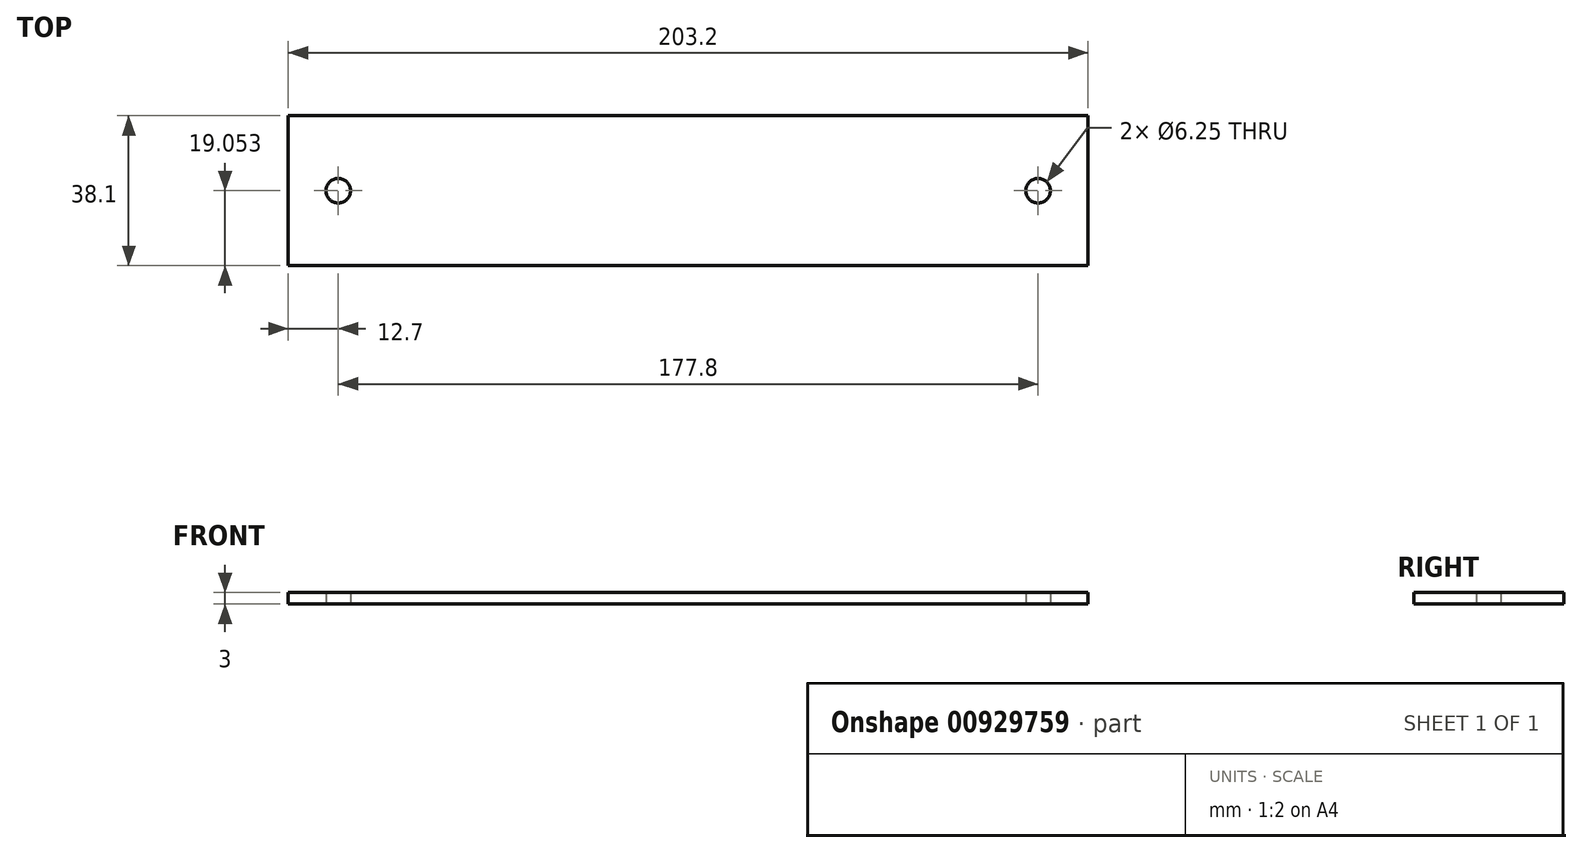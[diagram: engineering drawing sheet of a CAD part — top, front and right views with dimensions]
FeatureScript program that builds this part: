
annotation { "Feature Type Name" : "Feature", "Feature Type Description" : "" }
export const myFeature = defineFeature(function(context is Context, id is Id, definition is map)
    precondition{}
    {
        {
            var Q0;
            Q0=qCreatedBy(makeId("Top.planeOp"),FACE);
            var sketch = newSketch(context, id + "F0", { "sketchPlane" : qUnion([Q0])});
            skLineSegment(sketch, "E0.bottom", {"start": v(-107.28, 3.71) * mm, "end": v(95.92, 3.71) * mm});
            skLineSegment(sketch, "E0.top", {"start": v(-107.28, -34.39) * mm, "end": v(95.92, -34.39) * mm});
            skLineSegment(sketch, "E0.left", {"start": v(-107.28, 3.71) * mm, "end": v(-107.28, -34.39) * mm});
            skLineSegment(sketch, "E0.right", {"start": v(95.92, 3.71) * mm, "end": v(95.92, -34.39) * mm});
            skLineSegment(sketch, "E1", {"start": v(-107.28, -15.34) * mm, "end": v(95.92, -15.34) * mm});
            skPoint(sketch, "E2", {"position": v(-5.68, -15.34) * mm});
            skLineSegment(sketch, "E3", {"start": v(-5.68, -15.34) * mm, "end": v(95.92, -15.34) * mm});
            skPoint(sketch, "E4", {"position": v(45.12, -15.34) * mm});
            skLineSegment(sketch, "E5", {"start": v(45.12, -15.34) * mm, "end": v(95.92, -15.34) * mm});
            skPoint(sketch, "E6", {"position": v(70.52, -15.34) * mm});
            skLineSegment(sketch, "E7", {"start": v(70.52, -15.34) * mm, "end": v(95.92, -15.34) * mm});
            skPoint(sketch, "E8", {"position": v(83.22, -15.34) * mm});
            skCircle(sketch, "E9", {"center": v(83.22, -15.34) * mm, "radius": 3.12 * mm});
            skLineSegment(sketch, "E10", {"start": v(-5.68, -15.34) * mm, "end": v(-5.68, 3.71) * mm});
            skLineSegment(sketch, "E11", {"start": v(-5.68, 3.71) * mm, "end": v(-5.68, -34.39) * mm});
            skCircle(sketch, "E12.MirrorC", {"center": v(-94.58, -15.34) * mm, "radius": 3.12 * mm});
            skSolve(sketch);
        }
        {
            var Q0;
            {var subQ3=sQuery(id+"F0.wireOp",EDGE,"E10");Q0=makeQuery(id+"F0.imprint","IMPRINT",FACE,{"disambiguationData":[TD([[makeQuery(id+"F0.imprint","IMPRINT",EDGE,{"derivedFrom":subQ3}),-1.0]])]});}
            var Q1;
            {var subQ6=sQuery(id+"F0.wireOp",EDGE,"E11");Q1=makeQuery(id+"F0.imprint","IMPRINT",FACE,{"disambiguationData":[TD([[makeQuery(id+"F0.imprint","IMPRINT",EDGE,{"derivedFrom":subQ6}),-1.0]])]});}
            var Q2;
            {var subQ3=sQuery(id+"F0.wireOp",EDGE,"E11");Q2=makeQuery(id+"F0.imprint","IMPRINT",FACE,{"disambiguationData":[TD([[makeQuery(id+"F0.imprint","IMPRINT",EDGE,{"derivedFrom":subQ3}),1.0]])]});}
            var Q3;
            {var subQ7=sQuery(id+"F0.wireOp",EDGE,"E10");Q3=makeQuery(id+"F0.imprint","IMPRINT",FACE,{"disambiguationData":[TD([[makeQuery(id+"F0.imprint","IMPRINT",EDGE,{"derivedFrom":subQ7}),1.0]])]});}
            extrude(context, id + "F1", {"entities" : qUnion([Q0, Q1, Q2, Q3]), "depth" : 3 * mm, "offsetDistance" : 25 * mm});
        }
    });
